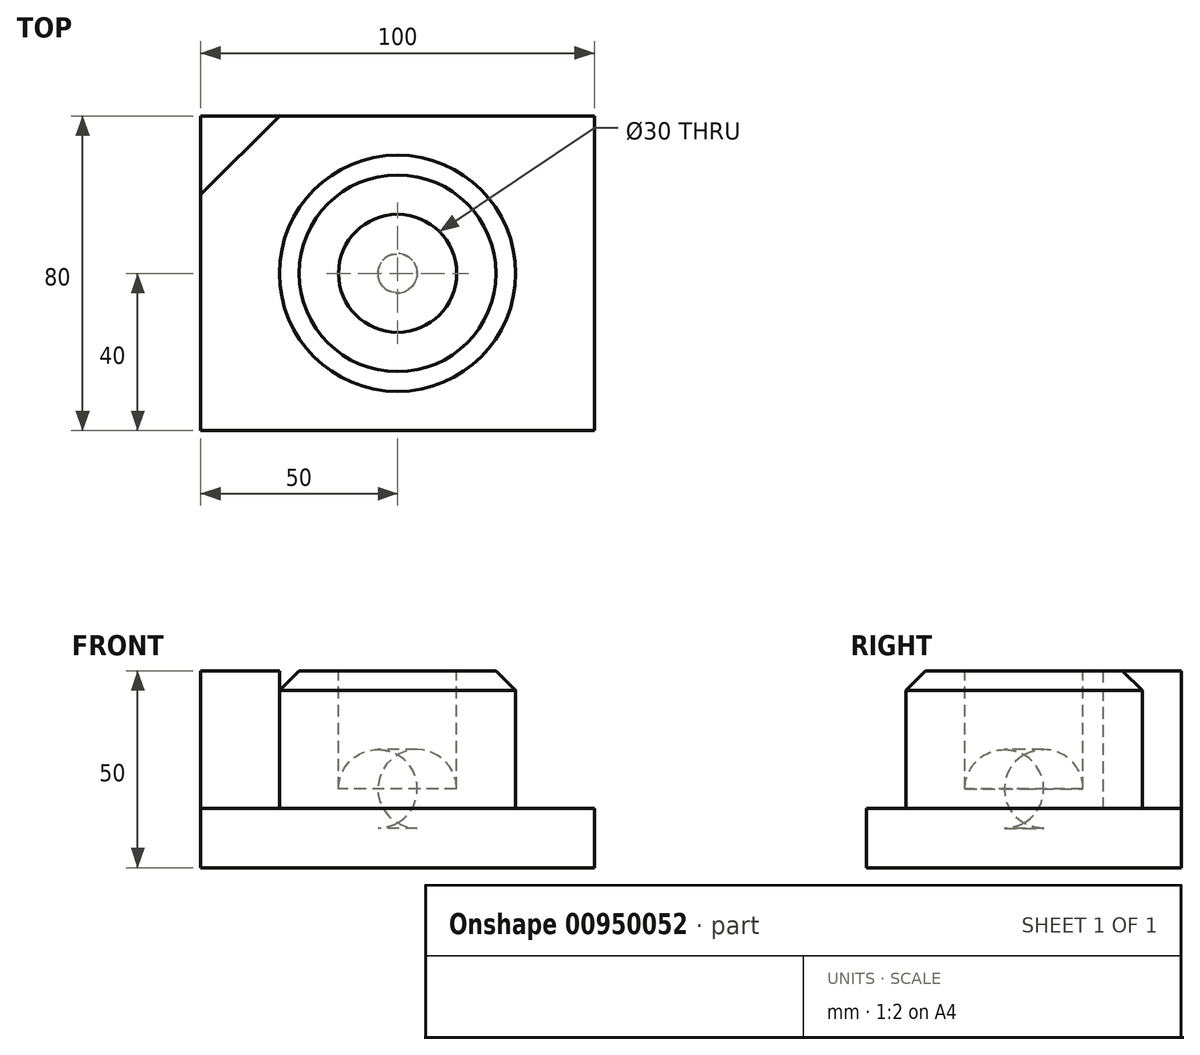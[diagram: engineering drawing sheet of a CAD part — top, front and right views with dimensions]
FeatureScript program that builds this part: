
annotation { "Feature Type Name" : "Feature", "Feature Type Description" : "" }
export const myFeature = defineFeature(function(context is Context, id is Id, definition is map)
    precondition{}
    {
        {
            var Q0;
            Q0=qCreatedBy(makeId("Top.planeOp"),FACE);
            var sketch = newSketch(context, id + "F0", { "sketchPlane" : qUnion([Q0])});
            skLineSegment(sketch, "E0.bottom", {"start": v(0, 0) * mm, "end": v(100, 0) * mm});
            skLineSegment(sketch, "E0.top", {"start": v(0, 80) * mm, "end": v(100, 80) * mm});
            skLineSegment(sketch, "E0.left", {"start": v(0, 0) * mm, "end": v(0, 80) * mm});
            skLineSegment(sketch, "E0.right", {"start": v(100, 0) * mm, "end": v(100, 80) * mm});
            skSolve(sketch);
        }
        {
            var Q0;
            Q0=makeQuery(id+"F0.imprint","IMPRINT",FACE,{"disambiguationData":[TD([[makeQuery(id+"F0.imprint","IMPRINT",EDGE,{"derivedFrom":sQuery(id+"F0.wireOp",EDGE,"E0.bottom")}),1.0]])]});
            extrude(context, id + "F1", {"entities" : qUnion([Q0]), "depth" : 15 * mm, "offsetDistance" : 25 * mm});
        }
        {
            var Q0;
            Q0=makeQuery(id+"F1.opExtrude","CAP_FACE",FACE,{"disambiguationData":[OSD([sQuery(id+"F0.wireOp",EDGE,"E0.bottom"),sQuery(id+"F0.wireOp",EDGE,"E0.top"),sQuery(id+"F0.wireOp",EDGE,"E0.left"),sQuery(id+"F0.wireOp",EDGE,"E0.right")])],"isStart":false});
            var sketch = newSketch(context, id + "F2", { "sketchPlane" : qUnion([Q0])});
            skLineSegment(sketch, "E1", {"start": v(0, 80) * mm, "end": v(0, 60) * mm});
            skLineSegment(sketch, "E2", {"start": v(0, 60) * mm, "end": v(20, 80) * mm});
            skLineSegment(sketch, "E3", {"start": v(20, 80) * mm, "end": v(0, 80) * mm});
            skSolve(sketch);
        }
        {
            var Q0;
            Q0 = qSketchRegion(id + "F2", true);
            extrude(context, id + "F3", {"entities" : qUnion([Q0]), "operationType" : NewBodyOperationType.ADD, "depth" : 35 * mm, "offsetDistance" : 25 * mm});
        }
        {
            var Q0;
            Q0=makeQuery(id+"F1.opExtrude","CAP_FACE",FACE,{"disambiguationData":[OSD([sQuery(id+"F0.wireOp",EDGE,"E0.bottom"),sQuery(id+"F0.wireOp",EDGE,"E0.top"),sQuery(id+"F0.wireOp",EDGE,"E0.left"),sQuery(id+"F0.wireOp",EDGE,"E0.right")])],"isStart":false});
            var sketch = newSketch(context, id + "F4", { "sketchPlane" : qUnion([Q0])});
            skCircle(sketch, "E4", {"center": v(50, 40) * mm, "radius": 30 * mm});
            skSolve(sketch);
        }
        {
            var Q0;
            Q0 = qSketchRegion(id + "F4", true);
            extrude(context, id + "F5", {"entities" : qUnion([Q0]), "operationType" : NewBodyOperationType.ADD, "depth" : 35 * mm, "offsetDistance" : 25 * mm});
        }
        {
            var Q0;
            Q0=makeQuery(id+"F5.opExtrude","CAP_EDGE",EDGE,{"disambiguationData":[OSD([sQuery(id+"F4.wireOp",EDGE,"E4")])],"isStart":false});
            chamfer(context, id + "F6", {"entities" : qUnion([Q0]), "width" : 5 * mm, "tangentPropagation" : true});
        }
        {
            var Q0;
            Q0=makeQuery(id+"F5.opExtrude","CAP_FACE",FACE,{"disambiguationData":[OSD([sQuery(id+"F4.wireOp",EDGE,"E4")])],"isStart":false});
            var sketch = newSketch(context, id + "F7", { "sketchPlane" : qUnion([Q0])});
            skCircle(sketch, "E5", {"center": v(50, 40) * mm, "radius": 15 * mm});
            skSolve(sketch);
        }
        {
            var Q0;
            Q0 = qSketchRegion(id + "F7", true);
            extrude(context, id + "F8", {"entities" : qUnion([Q0]), "operationType" : NewBodyOperationType.REMOVE, "oppositeDirection" : true, "depth" : 40 * mm, "offsetDistance" : 25 * mm});
        }
        {
            var Q0;
            Q0=makeQuery(id+"F8.boolean.opBoolean","COPY",EDGE,{"derivedFrom":makeQuery(id+"F8.opExtrude","CAP_EDGE",EDGE,{"disambiguationData":[OSD([sQuery(id+"F7.wireOp",EDGE,"E5")])],"isStart":false})});
            fillet(context, id + "F9", {"entities" : qUnion([Q0]), "radius" : 10 * mm, "tangentPropagation" : true, "allowEdgeOverflow" : false});
        }
    });
